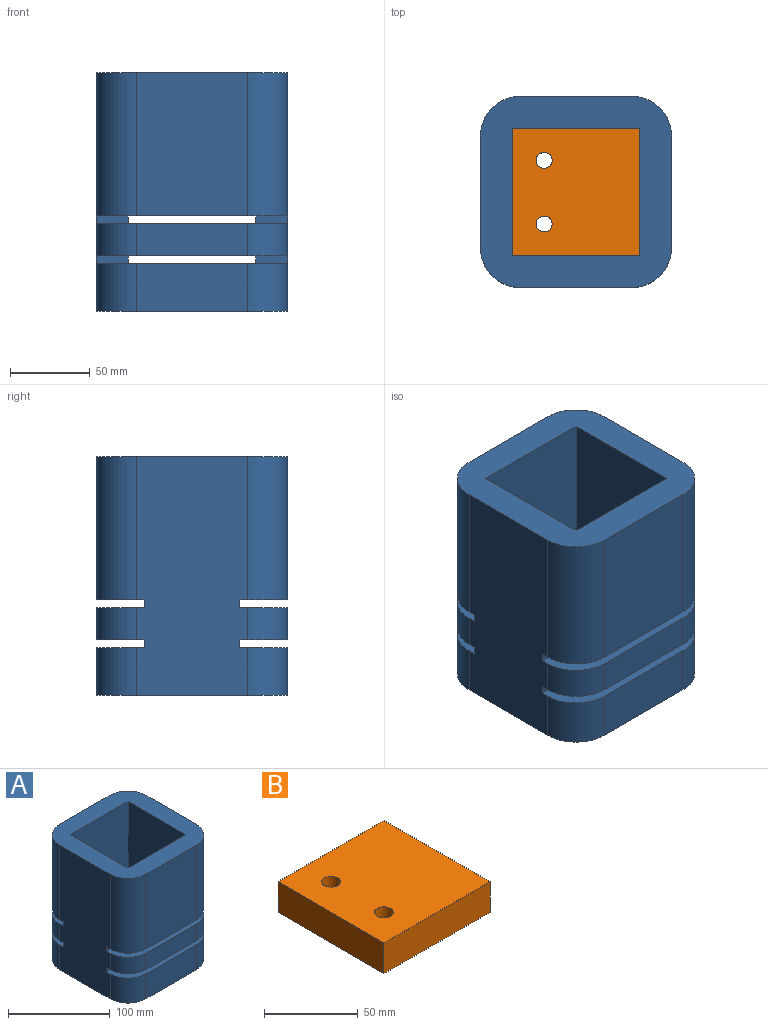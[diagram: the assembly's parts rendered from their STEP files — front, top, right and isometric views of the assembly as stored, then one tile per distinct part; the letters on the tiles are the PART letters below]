
ASSEMBLY  parts=2 mates=3
PART A: 46 faces, bbox 120x120x150 mm
  f0: plane 90x70mm, normal (0,1,0), area 6300mm2, adj f12,f14,f24,f43
  f1: plane 70x20mm, normal (0,1,0), area 1400mm2, adj f13,f15,f39,f44
  f2: plane 70x20mm, normal (0,-1,0), area 1400mm2, adj f17,f19,f31,f36
  f3: plane 90x70mm, normal (0,-1,0), area 6300mm2, adj f24,f28,f29,f32
  f4: plane 90x80mm, normal (0,-1,0), area 7200mm2, adj f6,f11,f24,f43
  f5: plane 80x20mm, normal (0,-1,0), area 1600mm2, adj f6,f11,f39,f44
  f6: plane 150x80mm, normal (-1,0,0), area 11800mm2, adj f4,f5,f7,f8,f20,f21,f24,f25
  f7: plane 80x30mm, normal (0,1,0), area 2400mm2, adj f6,f11,f25,f35
  f8: plane 80x20mm, normal (0,1,0), area 1600mm2, adj f6,f11,f31,f36
  f9: plane 150x70mm, normal (1,0,0), area 10400mm2, adj f12,f13,f18,f19,f24,f25,f26,f29
  f10: plane 150x70mm, normal (-1,0,0), area 10400mm2, adj f14,f15,f16,f17,f24,f25,f27,f28
  f11: plane 150x80mm, normal (1,0,0), area 11800mm2, adj f4,f5,f7,f8,f20,f21,f24,f25
  f12: cylinder r=25mm len=90mm, axis (0,0,1), area 3534.3mm2, adj f0,f9,f24,f43
  f13: cylinder r=25mm len=25mm, axis (0,0,1), area 785.4mm2, adj f1,f9,f39,f44
  f14: cylinder r=25mm len=90mm, axis (0,0,-1), area 3534.3mm2, adj f0,f10,f24,f43
  f15: cylinder r=25mm len=25mm, axis (0,0,-1), area 785.4mm2, adj f1,f10,f39,f44
  f16: cylinder r=25mm len=30mm, axis (0,0,1), area 1178.1mm2, adj f10,f23,f25,f35
  f17: cylinder r=25mm len=25mm, axis (0,0,1), area 785.4mm2, adj f2,f10,f31,f36
  f18: cylinder r=25mm len=30mm, axis (0,0,-1), area 1178.1mm2, adj f9,f23,f25,f35
  f19: cylinder r=25mm len=25mm, axis (0,0,-1), area 785.4mm2, adj f2,f9,f31,f36
  f20: plane 80x30mm, normal (0,-1,0), area 2400mm2, adj f6,f11,f25,f40
  f21: plane 90x80mm, normal (0,1,0), area 7200mm2, adj f6,f11,f24,f32
  f22: plane 70x30mm, normal (0,1,0), area 2100mm2, adj f25,f26,f27,f40
  f23: plane 70x30mm, normal (0,-1,0), area 2100mm2, adj f16,f18,f25,f35
  f24: plane 120x120mm, normal (0,0,1), area 7463.5mm2, adj f0,f3,f4,f6,f9,f10,f11,f12
  f25: plane 120x120mm, normal (0,0,-1), area 7463.5mm2, adj f6,f7,f9,f10,f11,f16,f18,f20
  f26: cylinder r=25mm len=30mm, axis (0,0,1), area 1178.1mm2, adj f9,f22,f25,f40
  f27: cylinder r=25mm len=30mm, axis (0,0,-1), area 1178.1mm2, adj f10,f22,f25,f40
  f28: cylinder r=25mm len=90mm, axis (0,0,1), area 3534.3mm2, adj f3,f10,f24,f32
  f29: cylinder r=25mm len=90mm, axis (0,0,-1), area 3534.3mm2, adj f3,f9,f24,f32
  f30: plane 20x5mm, normal (0,-1,0), area 100mm2, adj f6,f9,f31,f32
  f31: plane 120x30mm, normal (0,0,1), area 2531.7mm2, adj f2,f6,f8,f9,f10,f11,f17,f19
  f32: plane 120x30mm, normal (0,0,-1), area 2531.7mm2, adj f3,f6,f9,f10,f11,f21,f28,f29
  f33: plane 20x5mm, normal (0,-1,0), area 100mm2, adj f10,f11,f31,f32
  f34: plane 20x5mm, normal (0,-1,0), area 100mm2, adj f6,f9,f35,f36
  f35: plane 120x30mm, normal (0,0,1), area 2531.7mm2, adj f6,f7,f9,f10,f11,f16,f18,f23
  f36: plane 120x30mm, normal (0,0,-1), area 2531.7mm2, adj f2,f6,f8,f9,f10,f11,f17,f19
  f37: plane 20x5mm, normal (0,-1,0), area 100mm2, adj f10,f11,f35,f36
  f38: plane 20x5mm, normal (0,1,0), area 100mm2, adj f6,f9,f39,f40
  f39: plane 120x30mm, normal (0,0,-1), area 2531.7mm2, adj f1,f5,f6,f9,f10,f11,f13,f15
  f40: plane 120x30mm, normal (0,0,1), area 2531.7mm2, adj f6,f9,f10,f11,f20,f22,f26,f27
  f41: plane 20x5mm, normal (0,1,0), area 100mm2, adj f10,f11,f39,f40
  f42: plane 20x5mm, normal (0,1,0), area 100mm2, adj f6,f9,f43,f44
  f43: plane 120x30mm, normal (0,0,-1), area 2531.7mm2, adj f0,f4,f6,f9,f10,f11,f12,f14
  f44: plane 120x30mm, normal (0,0,1), area 2531.7mm2, adj f1,f5,f6,f9,f10,f11,f13,f15
  f45: plane 20x5mm, normal (0,1,0), area 100mm2, adj f10,f11,f43,f44
PART B: 8 faces, bbox 80x80x20 mm
  f0: plane 80x20mm, normal (1,0,0), area 1600mm2, adj f1,f3,f4,f5
  f1: plane 80x20mm, normal (0,1,0), area 1600mm2, adj f0,f2,f4,f5
  f2: plane 80x20mm, normal (-1,0,0), area 1600mm2, adj f1,f3,f4,f5
  f3: plane 80x20mm, normal (0,-1,0), area 1600mm2, adj f0,f2,f4,f5
  f4: plane 80x80mm, normal (0,0,1), area 6242.9mm2, adj f0,f1,f2,f3,f6,f7
  f5: plane 80x80mm, normal (0,0,-1), area 6242.9mm2, adj f0,f1,f2,f3,f6,f7
  f6: cylinder r=5mm len=20mm, axis (0,0,1), area 628.3mm2, adj f4,f5
  f7: cylinder r=5mm len=20mm, axis (0,0,1), area 628.3mm2, adj f4,f5
PLACE A t=(-23.83,-52.68,-18.98)mm
PLACE B t=(-23.83,-52.68,-13.98)mm
MATE planar B.f3 <-> A.f7  axis (0,-1,0) through (-23.83,-92.68,-3.98)mm
MATE planar B.f5 <-> A.f12  axis (0,0,-1) through (-23.33,-52.68,-13.98)mm
MATE planar A.f11 <-> B.f2  axis (1,0,0) through (-63.83,-52.68,-18.98)mm
